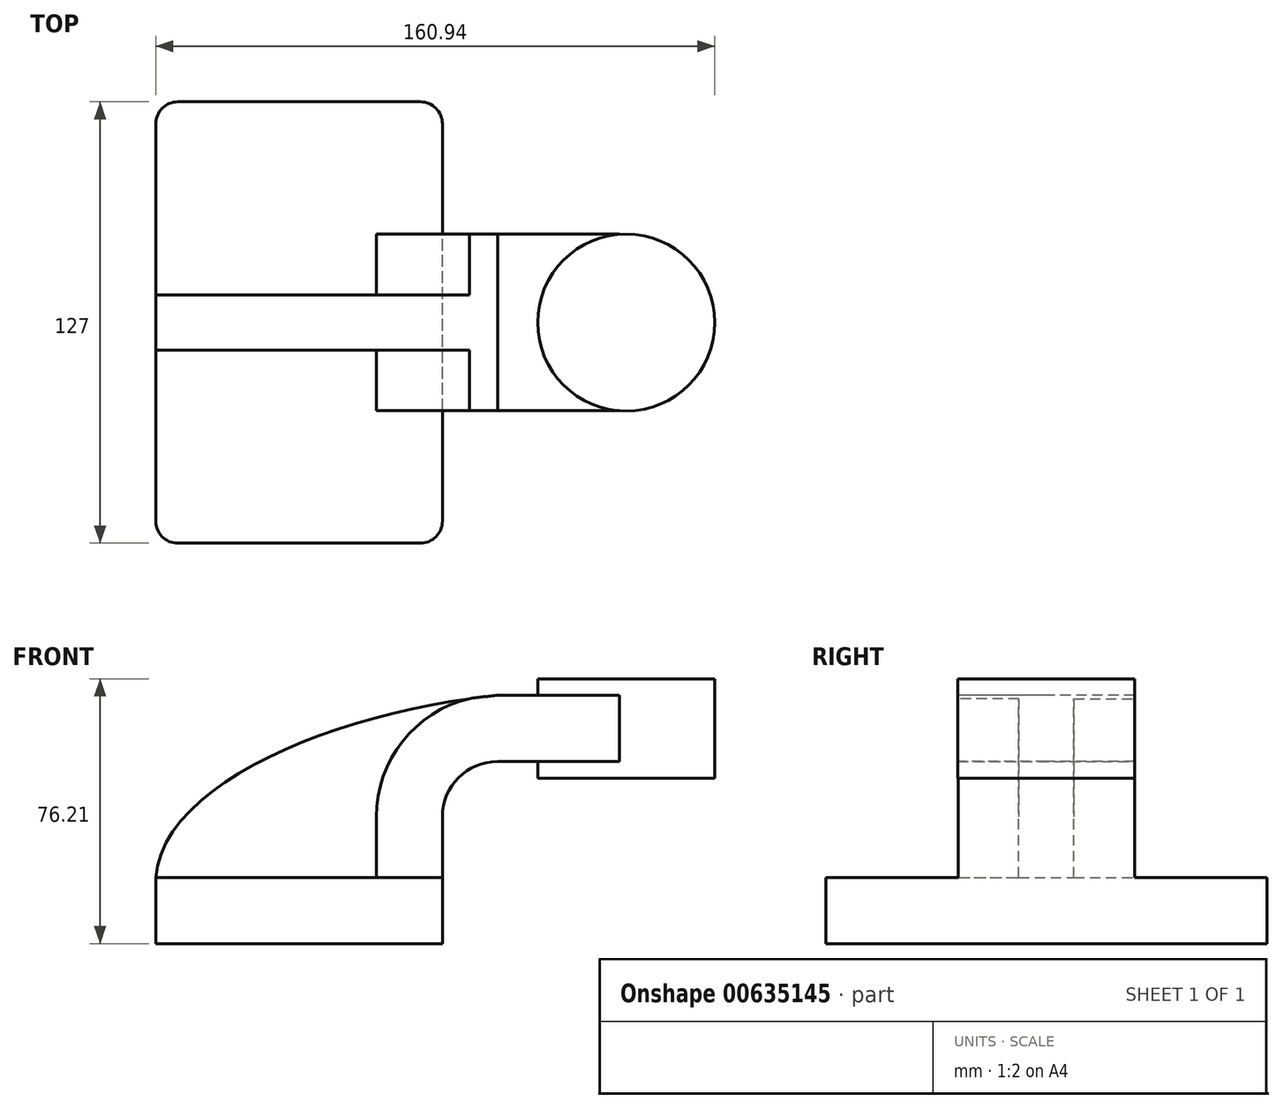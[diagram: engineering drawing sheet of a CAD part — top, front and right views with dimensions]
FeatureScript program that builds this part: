
annotation { "Feature Type Name" : "Feature", "Feature Type Description" : "" }
export const myFeature = defineFeature(function(context is Context, id is Id, definition is map)
    precondition{}
    {
        {
            var Q0;
            Q0=qCreatedBy(makeId("Front.planeOp"),FACE);
            var sketch = newSketch(context, id + "F0", { "sketchPlane" : qUnion([Q0])});
            skLineSegment(sketch, "E0.bottom", {"start": v(-41.27, -9.53) * mm, "end": v(41.28, -9.53) * mm});
            skLineSegment(sketch, "E0.top", {"start": v(-41.28, 9.53) * mm, "end": v(41.28, 9.53) * mm});
            skLineSegment(sketch, "E0.left", {"start": v(-41.28, -9.53) * mm, "end": v(-41.28, 9.53) * mm});
            skLineSegment(sketch, "E0.right", {"start": v(41.28, -9.53) * mm, "end": v(41.28, 9.53) * mm});
            skPoint(sketch, "E0.middle", {"position": v(0, 0) * mm});
            skLineSegment(sketch, "E1.bottom", {"start": v(68.86, 38.1) * mm, "end": v(119.66, 38.1) * mm});
            skLineSegment(sketch, "E1.top", {"start": v(68.86, 66.67) * mm, "end": v(119.66, 66.67) * mm});
            skLineSegment(sketch, "E1.left", {"start": v(68.86, 38.1) * mm, "end": v(68.86, 66.67) * mm});
            skLineSegment(sketch, "E1.right", {"start": v(119.66, 38.1) * mm, "end": v(119.66, 66.67) * mm});
            skPoint(sketch, "E1.middle", {"position": v(94.26, 52.39) * mm});
            skLineSegment(sketch, "E2", {"start": v(41.27, 9.53) * mm, "end": v(41.27, 27) * mm});
            skArc(sketch, "E3", {"start": v(41.27, 27) * mm, "mid": v(45.92, 38.22) * mm, "end": v(57.15, 42.87) * mm});
            skLineSegment(sketch, "E4.0", {"start": v(57.15, 61.92) * mm, "end": v(94.18, 61.93) * mm});
            skArc(sketch, "E4.1", {"start": v(22.22, 27) * mm, "mid": v(32.45, 51.69) * mm, "end": v(57.15, 61.92) * mm});
            skLineSegment(sketch, "E4.2", {"start": v(22.22, 9.53) * mm, "end": v(22.22, 27) * mm});
            skFitSpline(sketch, "E5", {"points": [v(-41.27, 9.52) * mm, v(57.15, 61.92) * mm], "startDerivative": vector(7.08, 84.64) * mm, "endDerivative": vector(130.48, 12.64) * mm});
            skLineSegment(sketch, "E6", {"start": v(57.15, 42.87) * mm, "end": v(94.18, 42.87) * mm});
            skLineSegment(sketch, "E7", {"start": v(94.18, 38.1) * mm, "end": v(94.18, 66.67) * mm});
            skPoint(sketch, "E7.startSnap0", {"position": v(94.26, 38.1) * mm});
            skSolve(sketch);
        }
        {
            var Q0;
            Q0=makeQuery(id+"F0.imprint","IMPRINT",FACE,{"disambiguationData":[TD([[makeQuery(id+"F0.imprint","IMPRINT",EDGE,{"derivedFrom":sQuery(id+"F0.wireOp",EDGE,"E0.bottom")}),1.0]])]});
            extrude(context, id + "F1", {"entities" : qUnion([Q0]), "endBound" : BoundingType.SYMMETRIC, "depth" : 127 * mm, "offsetDistance" : 25.4 * mm});
        }
        {
            var Q0;
            {var subQ1=sQuery(id+"F0.wireOp",EDGE,"E2");Q0=makeQuery(id+"F0.imprint","IMPRINT",FACE,{"disambiguationData":[TD([[makeQuery(id+"F0.imprint","IMPRINT",EDGE,{"derivedFrom":subQ1}),1.0]])]});}
            var Q1;
            {var subQ0=sQuery(id+"F0.wireOp",EDGE,"E6");var subQ1=sQuery(id+"F0.wireOp",EDGE,"E1.left");var subQ2=makeQuery(id+"F0.imprint","INTERSECT",VERTEX,{"derivedFrom":[subQ1,subQ0]});Q1=makeQuery(id+"F0.imprint","IMPRINT",FACE,{"disambiguationData":[TD([[makeQuery(id+"F0.imprint","IMPRINT",EDGE,{"disambiguationData":[TD([[subQ2,-1.0]])],"derivedFrom":subQ1}),-1.0]])]});}
            extrude(context, id + "F2", {"entities" : qUnion([Q0, Q1]), "operationType" : NewBodyOperationType.ADD, "endBound" : BoundingType.SYMMETRIC, "depth" : 50.8 * mm, "offsetDistance" : 25.4 * mm});
        }
        {
            var Q0;
            {var subQ3=sQuery(id+"F0.wireOp",EDGE,"E4.2");Q0=makeQuery(id+"F0.imprint","IMPRINT",FACE,{"disambiguationData":[TD([[makeQuery(id+"F0.imprint","IMPRINT",EDGE,{"derivedFrom":subQ3}),1.0]])]});}
            extrude(context, id + "F3", {"entities" : qUnion([Q0]), "operationType" : NewBodyOperationType.ADD, "endBound" : BoundingType.SYMMETRIC, "depth" : 15.88 * mm, "offsetDistance" : 25.4 * mm});
        }
        {
            var Q0;
            {var subQ4=sQuery(id+"F0.wireOp",EDGE,"E1.right");Q0=makeQuery(id+"F0.imprint","IMPRINT",FACE,{"disambiguationData":[TD([[makeQuery(id+"F0.imprint","IMPRINT",EDGE,{"derivedFrom":subQ4}),1.0]])]});}
            var Q1;
            Q1=sQuery(id+"F0.wireOp",EDGE,"E7");
            revolve(context, id + "F4", {"operationType" : NewBodyOperationType.ADD, "entities" : qUnion([Q0]), "axis" : qUnion([Q1]), "revolveType" : RevolveType.FULL});
        }
        {
            var Q0;
            Q0=makeQuery(id+"F1.opExtrude","CAP_EDGE",EDGE,{"disambiguationData":[OSD([sQuery(id+"F0.wireOp",EDGE,"E0.left")])],"isStart":false});
            var Q1;
            Q1=makeQuery(id+"F1.opExtrude","CAP_EDGE",EDGE,{"disambiguationData":[OSD([sQuery(id+"F0.wireOp",EDGE,"E0.right")])],"isStart":false});
            var Q2;
            Q2=makeQuery(id+"F1.opExtrude","CAP_EDGE",EDGE,{"disambiguationData":[OSD([sQuery(id+"F0.wireOp",EDGE,"E0.right")])],"isStart":true});
            var Q3;
            Q3=makeQuery(id+"F1.opExtrude","CAP_EDGE",EDGE,{"disambiguationData":[OSD([sQuery(id+"F0.wireOp",EDGE,"E0.left")])],"isStart":true});
            fillet(context, id + "F5", {"entities" : qUnion([Q0, Q1, Q2, Q3]), "radius" : 6.35 * mm, "tangentPropagation" : true, "allowEdgeOverflow" : false});
        }
    });
